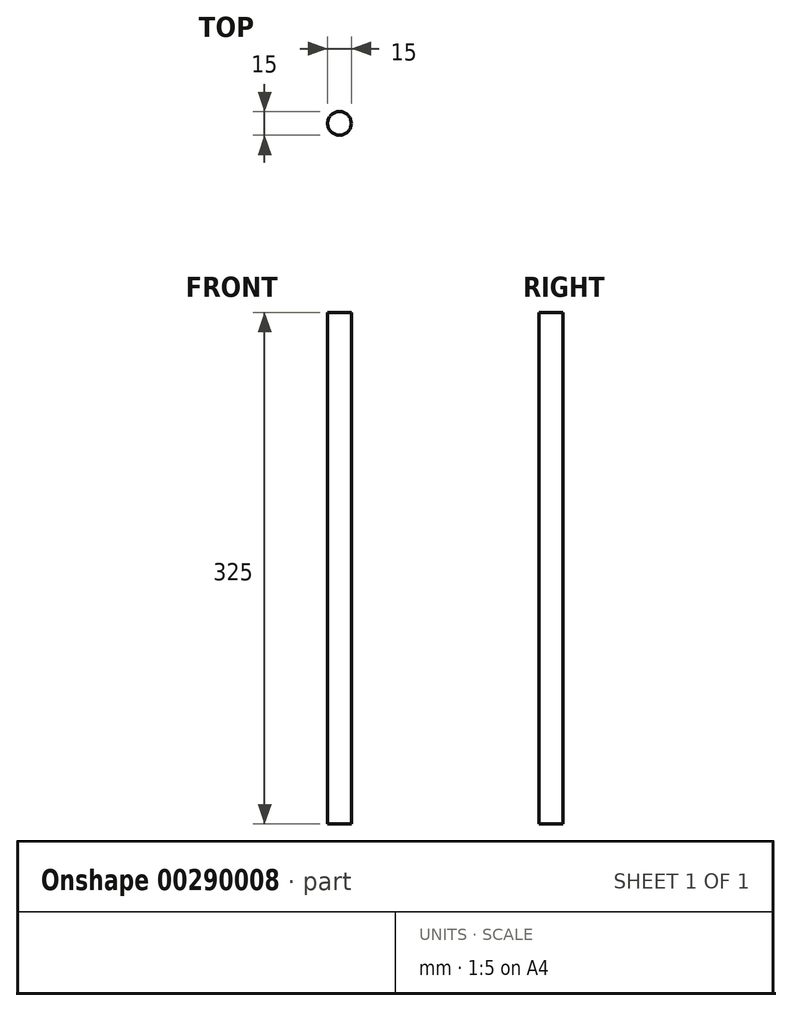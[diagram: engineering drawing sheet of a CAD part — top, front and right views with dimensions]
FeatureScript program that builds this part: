
annotation { "Feature Type Name" : "Feature", "Feature Type Description" : "" }
export const myFeature = defineFeature(function(context is Context, id is Id, definition is map)
    precondition{}
    {
        {
            var Q0;
            Q0=qCreatedBy(makeId("Top.planeOp"),FACE);
            var sketch = newSketch(context, id + "F0", { "sketchPlane" : qUnion([Q0])});
            skCircle(sketch, "E0", {"center": v(0, 0) * mm, "radius": 7.5 * mm});
            skSolve(sketch);
        }
        {
            var Q0;
            Q0=makeQuery(id+"F0.imprint","IMPRINT",FACE,{"disambiguationData":[TD([[makeQuery(id+"F0.imprint","IMPRINT",EDGE,{"derivedFrom":sQuery(id+"F0.wireOp",EDGE,"E0")}),1.0]])]});
            extrude(context, id + "F1", {"entities" : qUnion([Q0]), "depth" : 325 * mm});
        }
    });
